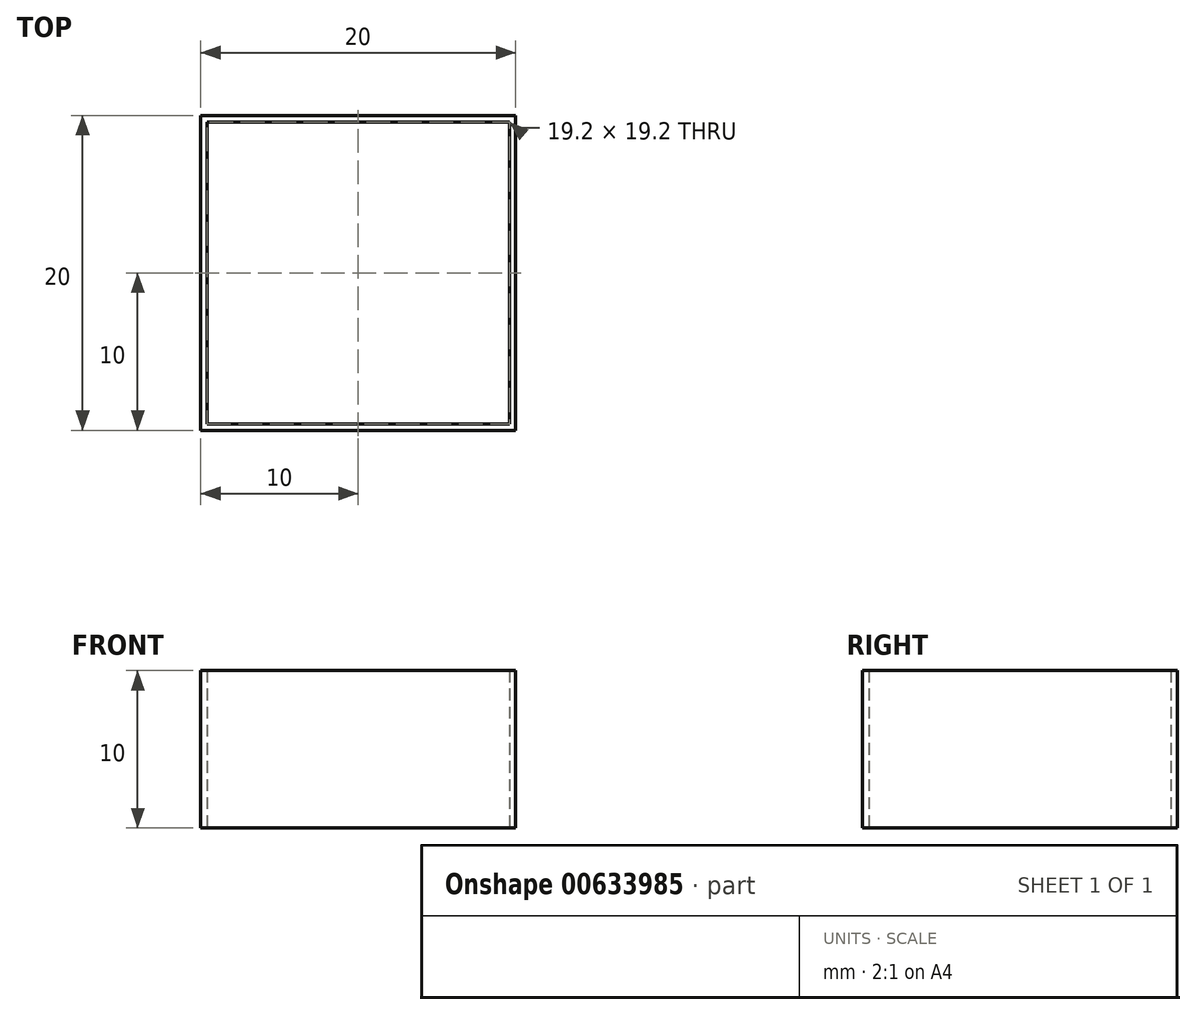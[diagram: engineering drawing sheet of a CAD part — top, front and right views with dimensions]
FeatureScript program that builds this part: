
annotation { "Feature Type Name" : "Feature", "Feature Type Description" : "" }
export const myFeature = defineFeature(function(context is Context, id is Id, definition is map)
    precondition{}
    {
        {
            var Q0;
            Q0=qCreatedBy(makeId("Top.planeOp"),FACE);
            var sketch = newSketch(context, id + "F0", { "sketchPlane" : qUnion([Q0])});
            skLineSegment(sketch, "E0.bottom", {"start": v(10, 10) * mm, "end": v(-10, 10) * mm});
            skLineSegment(sketch, "E0.top", {"start": v(10, -10) * mm, "end": v(-10, -10) * mm});
            skLineSegment(sketch, "E0.left", {"start": v(10, 10) * mm, "end": v(10, -10) * mm});
            skLineSegment(sketch, "E0.right", {"start": v(-10, 10) * mm, "end": v(-10, -10) * mm});
            skPoint(sketch, "E0.middle", {"position": v(0, 0) * mm});
            skSolve(sketch);
        }
        {
            var Q0;
            Q0=makeQuery(id+"F0.imprint","IMPRINT",FACE,{"disambiguationData":[TD([[makeQuery(id+"F0.imprint","IMPRINT",EDGE,{"derivedFrom":sQuery(id+"F0.wireOp",EDGE,"E0.bottom")}),1.0]])]});
            extrude(context, id + "F1", {"entities" : qUnion([Q0]), "depth" : 10 * mm, "offsetDistance" : 25 * mm});
        }
        {
            var Q0;
            Q0=makeQuery(id+"F1.opExtrude","CAP_FACE",FACE,{"disambiguationData":[OSD([sQuery(id+"F0.wireOp",EDGE,"E0.bottom"),sQuery(id+"F0.wireOp",EDGE,"E0.top"),sQuery(id+"F0.wireOp",EDGE,"E0.left"),sQuery(id+"F0.wireOp",EDGE,"E0.right")])],"isStart":false});
            var Q1;
            Q1=makeQuery(id+"F1.opExtrude","CAP_FACE",FACE,{"disambiguationData":[OSD([sQuery(id+"F0.wireOp",EDGE,"E0.bottom"),sQuery(id+"F0.wireOp",EDGE,"E0.top"),sQuery(id+"F0.wireOp",EDGE,"E0.left"),sQuery(id+"F0.wireOp",EDGE,"E0.right")])],"isStart":true});
            shell(context, id + "F2", {"entities" : qUnion([Q0, Q1]), "thickness" : .4 * mm});
        }
    });
